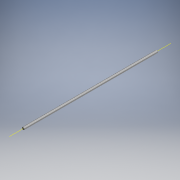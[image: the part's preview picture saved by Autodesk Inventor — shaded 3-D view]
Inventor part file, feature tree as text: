
AUTODESK INVENTOR PART (.ipt)
format: ipt  version: 2019 (Build 230136000, 136)  size: 111,616 bytes
history: native  units: mm (DEFAULTED — no unit token found)
features: extrude x1, fillet x1, sketch x1
ambient origin geometry x8: Origin, YZ Plane, XZ Plane, XY Plane, X Axis, Y Axis, Z Axis, Center Point
bodies: Solid1 (feature_tree)
feature tree (3):
  extrude  "Extrusion1"  TaperAngle=30.0deg  [1 undecoded]
  fillet  "Fillet1"  [1 undecoded]
  sketch  "Sketch1"  dims[d0=5.7658mm d1=30.0deg d2=120.0deg d3=2.883139mm d4=304.8mm d5=0.0mm d6=0.1mm d7=2.883139mm]
note: 2 required parameter values undecoded (feature->parameter linkage not recoverable at this tier; creation-order binding heuristic only, values carry confidence <= 0.55)
